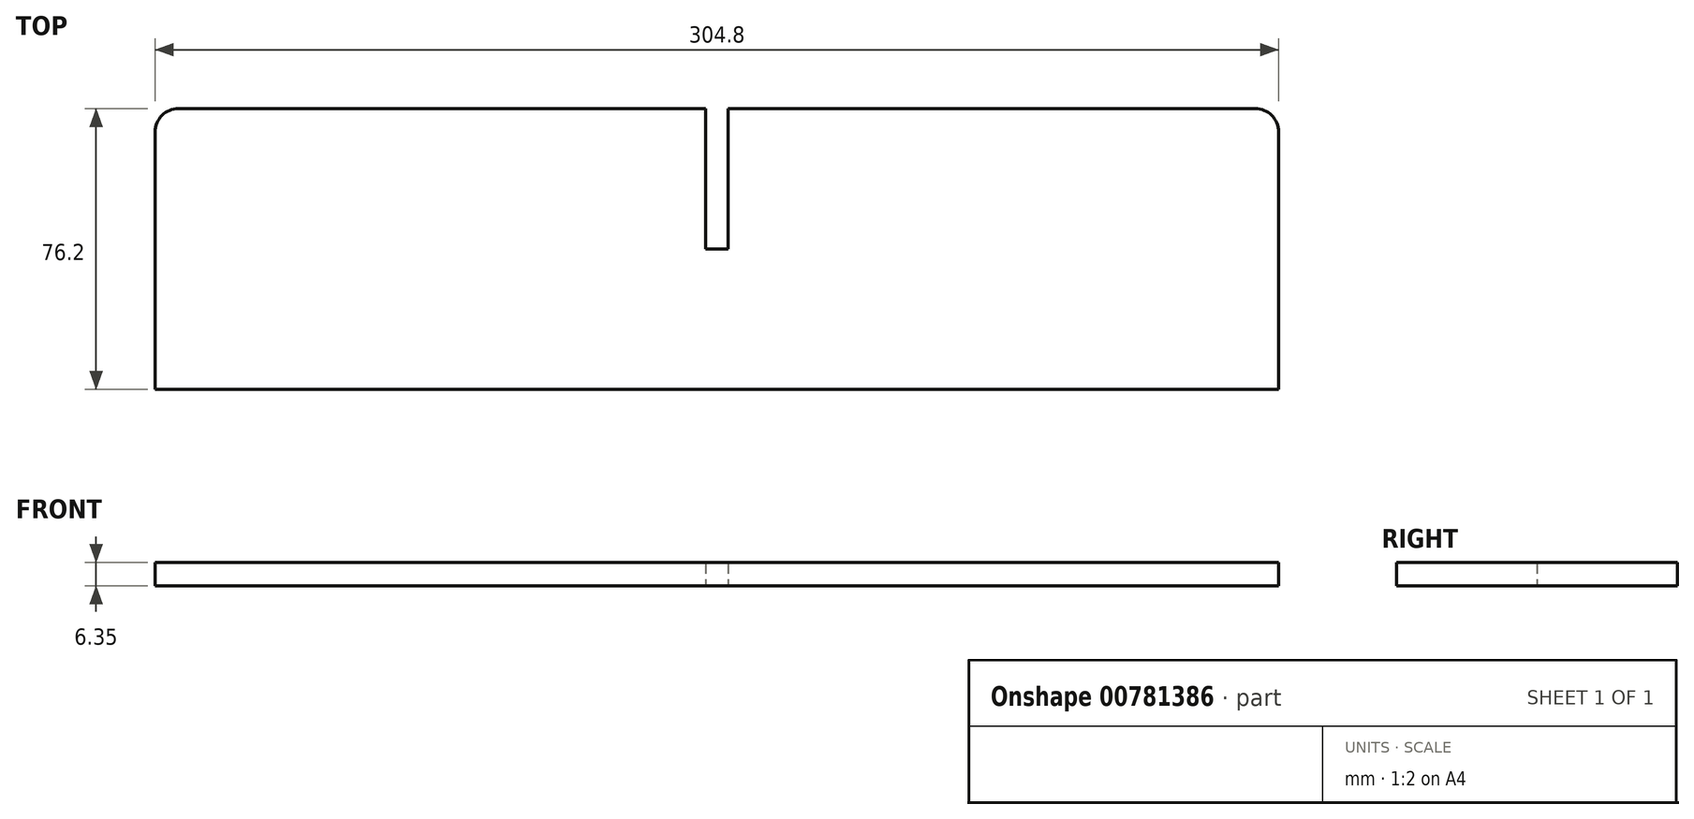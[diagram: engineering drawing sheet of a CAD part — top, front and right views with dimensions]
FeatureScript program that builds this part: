
annotation { "Feature Type Name" : "Feature", "Feature Type Description" : "" }
export const myFeature = defineFeature(function(context is Context, id is Id, definition is map)
    precondition{}
    {
        {
            var Q0;
            Q0=qCreatedBy(makeId("Top.planeOp"),FACE);
            var sketch = newSketch(context, id + "F0", { "sketchPlane" : qUnion([Q0])});
            skLineSegment(sketch, "E0.bottom", {"start": v(-146.05, 23.15) * mm, "end": v(-3, 23.15) * mm});
            skLineSegment(sketch, "E0.top", {"start": v(-152.4, -53.05) * mm, "end": v(152.4, -53.05) * mm});
            skLineSegment(sketch, "E0.left", {"start": v(-152.4, 16.8) * mm, "end": v(-152.4, -53.05) * mm});
            skLineSegment(sketch, "E0.right", {"start": v(152.4, 16.8) * mm, "end": v(152.4, -53.05) * mm});
            skPoint(sketch, "E1", {"position": v(0, 23.15) * mm});
            skLineSegment(sketch, "E2.top", {"start": v(-3, -14.95) * mm, "end": v(3, -14.95) * mm});
            skLineSegment(sketch, "E2.left", {"start": v(-3, 23.15) * mm, "end": v(-3, -14.95) * mm});
            skLineSegment(sketch, "E2.right", {"start": v(3, 23.15) * mm, "end": v(3, -14.95) * mm});
            skPoint(sketch, "E3", {"position": v(0, -14.95) * mm});
            skLineSegment(sketch, "E4.trimOffspring", {"start": v(3, 23.15) * mm, "end": v(146.05, 23.15) * mm});
            skPoint(sketch, "E5.visualSharp", {"position": v(-152.4, 23.15) * mm});
            skArc(sketch, "E5.filletArc", {"start": v(-146.05, 23.15) * mm, "mid": v(-150.54, 21.3) * mm, "end": v(-152.4, 16.8) * mm});
            skPoint(sketch, "E6.visualSharp", {"position": v(152.4, 23.15) * mm});
            skArc(sketch, "E6.filletArc", {"start": v(152.4, 16.8) * mm, "mid": v(150.54, 21.3) * mm, "end": v(146.05, 23.15) * mm});
            skSolve(sketch);
        }
        {
            var Q0;
            Q0 = qSketchRegion(id + "F0", true);
            extrude(context, id + "F1", {"entities" : qUnion([Q0]), "depth" : 6.35 * mm, "offsetDistance" : 25.4 * mm});
        }
    });
